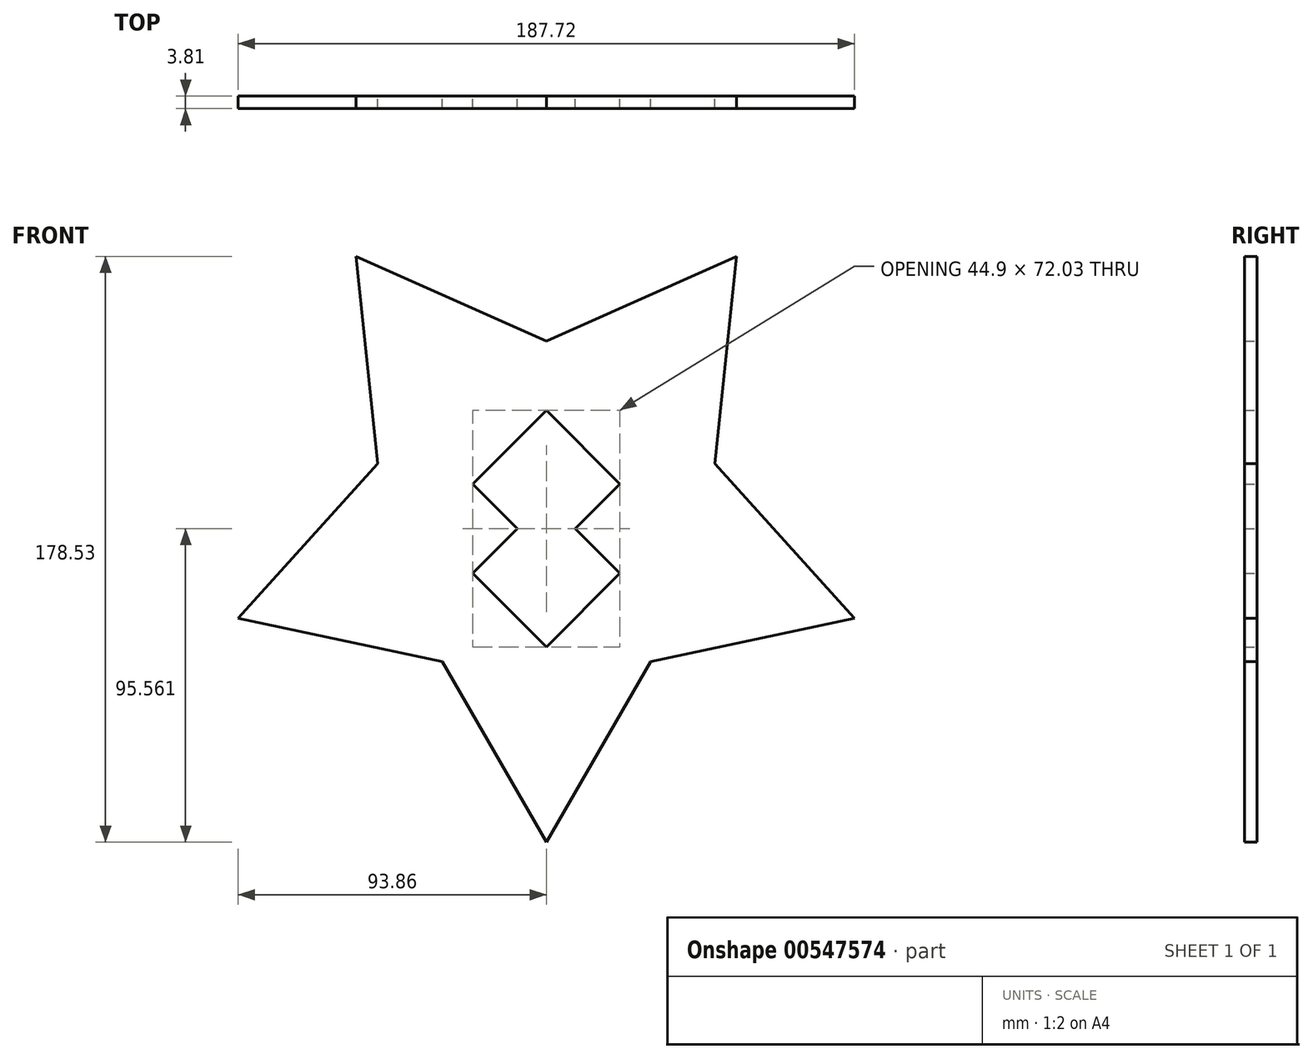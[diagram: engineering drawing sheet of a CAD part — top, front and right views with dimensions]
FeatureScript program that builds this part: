
annotation { "Feature Type Name" : "Feature", "Feature Type Description" : "" }
export const myFeature = defineFeature(function(context is Context, id is Id, definition is map)
    precondition{}
    {
        {
            var Q0;
            Q0=qCreatedBy(makeId("Front.planeOp"),FACE);
            var sketch = newSketch(context, id + "F0", { "sketchPlane" : qUnion([Q0])});
            skLineSegment(sketch, "E0", {"start": v(0, 57.55) * mm, "end": v(58.01, 83.37) * mm});
            skLineSegment(sketch, "E1", {"start": v(58.01, 83.37) * mm, "end": v(51.37, 20.22) * mm});
            skLineSegment(sketch, "E2", {"start": v(51.37, 20.22) * mm, "end": v(93.86, -26.97) * mm});
            skLineSegment(sketch, "E3", {"start": v(93.86, -26.97) * mm, "end": v(31.75, -40.17) * mm});
            skLineSegment(sketch, "E4", {"start": v(-51.37, 20.22) * mm, "end": v(-93.86, -26.97) * mm});
            skLineSegment(sketch, "E5", {"start": v(-93.86, -26.97) * mm, "end": v(-31.75, -40.17) * mm});
            skLineSegment(sketch, "E6", {"start": v(-51.37, 20.22) * mm, "end": v(-58.01, 83.37) * mm});
            skLineSegment(sketch, "E7", {"start": v(-58.01, 83.37) * mm, "end": v(0, 57.55) * mm});
            skLineSegment(sketch, "E8", {"start": v(-31.75, -40.17) * mm, "end": v(0, -95.16) * mm});
            skLineSegment(sketch, "E9", {"start": v(0, -95.16) * mm, "end": v(31.75, -40.17) * mm});
            skLineSegment(sketch, "E10", {"start": v(0, -8.48) * mm, "end": v(-22.45, 13.97) * mm});
            skLineSegment(sketch, "E11", {"start": v(-22.45, 13.97) * mm, "end": v(0, 36.42) * mm});
            skLineSegment(sketch, "E12", {"start": v(0, 9.29) * mm, "end": v(-22.45, -13.17) * mm});
            skLineSegment(sketch, "E13", {"start": v(-22.45, -13.17) * mm, "end": v(0, -35.62) * mm});
            skLineSegment(sketch, "E14", {"start": v(22.45, -13.17) * mm, "end": v(0, -35.62) * mm});
            skLineSegment(sketch, "E15", {"start": v(0, 9.29) * mm, "end": v(22.45, -13.17) * mm});
            skLineSegment(sketch, "E16", {"start": v(0, 36.42) * mm, "end": v(22.45, 13.97) * mm});
            skLineSegment(sketch, "E17", {"start": v(22.45, 13.97) * mm, "end": v(0, -8.48) * mm});
            skSolve(sketch);
        }
        {
            var Q0;
            Q0=makeQuery(id+"F0.imprint","IMPRINT",FACE,{"disambiguationData":[TD([[makeQuery(id+"F0.imprint","IMPRINT",EDGE,{"derivedFrom":sQuery(id+"F0.wireOp",EDGE,"E0")}),-1.0]])]});
            extrude(context, id + "F1", {"entities" : qUnion([Q0]), "depth" : 3.8 * mm, "offsetDistance" : 25.4 * mm});
        }
    });
